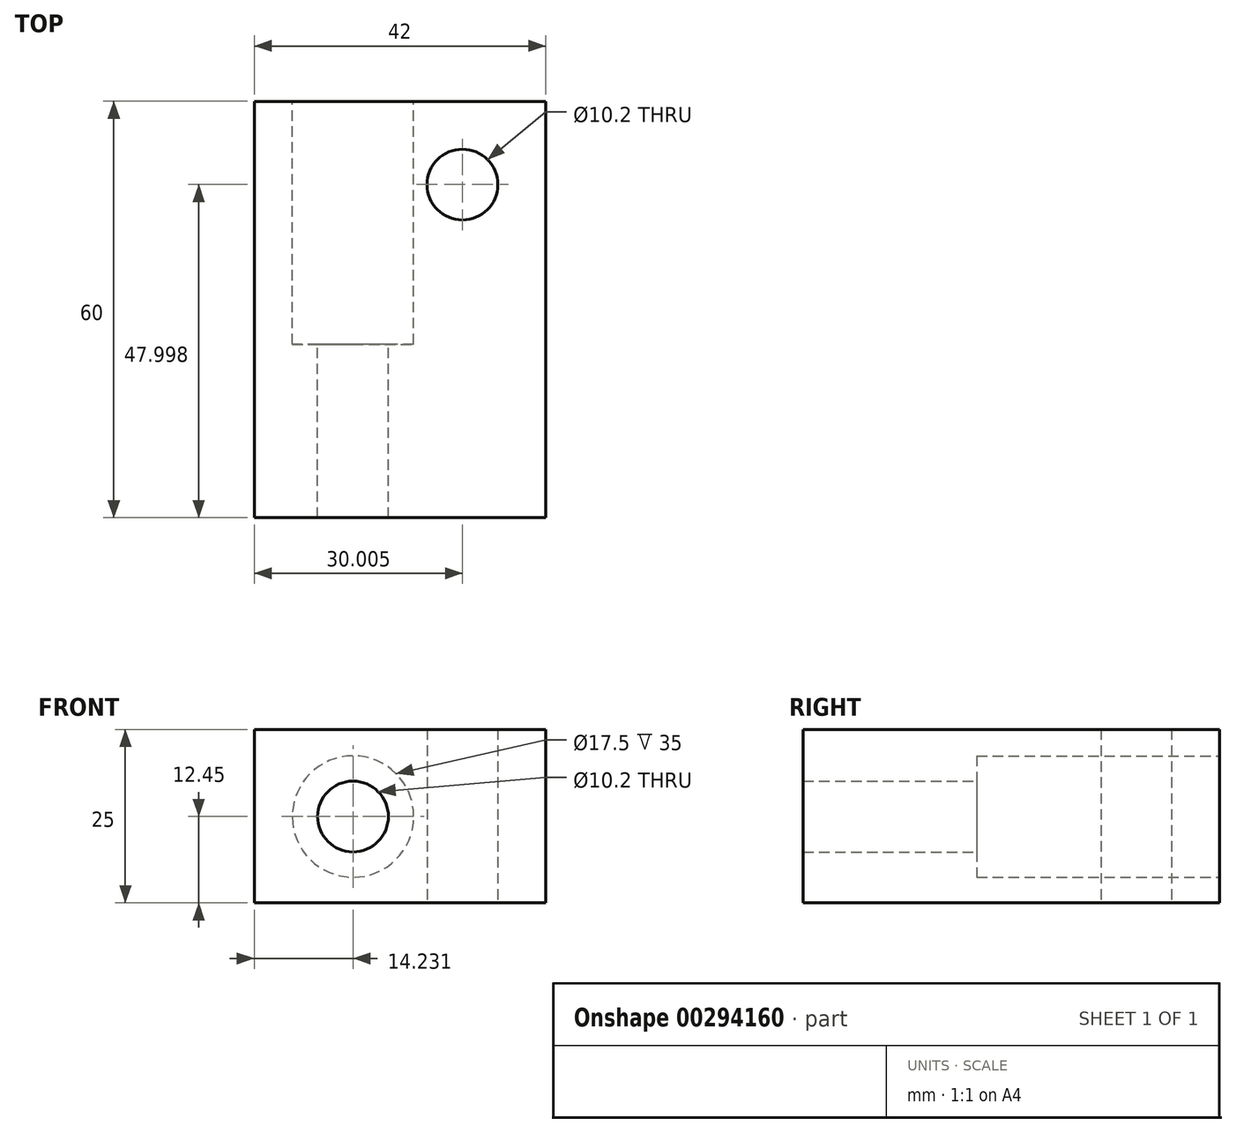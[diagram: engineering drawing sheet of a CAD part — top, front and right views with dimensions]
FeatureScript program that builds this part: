
annotation { "Feature Type Name" : "Feature", "Feature Type Description" : "" }
export const myFeature = defineFeature(function(context is Context, id is Id, definition is map)
    precondition{}
    {
        {
            var Q0;
            Q0=qCreatedBy(makeId("Top.planeOp"),FACE);
            var sketch = newSketch(context, id + "F0", { "sketchPlane" : qUnion([Q0])});
            skLineSegment(sketch, "E0", {"start": v(-36.42, -11.14) * mm, "end": v(5.58, -11.14) * mm});
            skLineSegment(sketch, "E1", {"start": v(5.58, -11.14) * mm, "end": v(5.58, 48.86) * mm});
            skLineSegment(sketch, "E2", {"start": v(5.58, 48.86) * mm, "end": v(-36.42, 48.86) * mm});
            skLineSegment(sketch, "E3", {"start": v(-36.42, 48.86) * mm, "end": v(-36.42, -11.14) * mm});
            skLineSegment(sketch, "E4", {"start": v(5.58, 48.86) * mm, "end": v(-6.42, 48.86) * mm});
            skLineSegment(sketch, "E5", {"start": v(-6.42, 48.86) * mm, "end": v(-6.42, 36.86) * mm, "construction": true});
            skCircle(sketch, "E6", {"center": v(-6.42, 36.86) * mm, "radius": 5.1 * mm});
            skSolve(sketch);
        }
        {
            var Q0;
            Q0=makeQuery(id+"F0.imprint","IMPRINT",FACE,{"disambiguationData":[TD([[makeQuery(id+"F0.imprint","IMPRINT",EDGE,{"derivedFrom":sQuery(id+"F0.wireOp",EDGE,"E0")}),1.0]])]});
            extrude(context, id + "F1", {"entities" : qUnion([Q0]), "depth" : 25 * mm});
        }
        {
            var Q0;
            Q0=makeQuery(id+"F1.opExtrude","SWEPT_FACE",FACE,{"disambiguationData":[OSD([sQuery(id+"F0.wireOp",EDGE,"E2"),sQuery(id+"F0.wireOp",EDGE,"E4")])]});
            var sketch = newSketch(context, id + "F2", { "sketchPlane" : qUnion([Q0])});
            skCircle(sketch, "E7", {"center": v(22.19, 12.45) * mm, "radius": 8.75 * mm});
            skCircle(sketch, "E8", {"center": v(22.19, 12.45) * mm, "radius": 5.1 * mm});
            skSolve(sketch);
        }
        {
            var Q0;
            Q0 = qSketchRegion(id + "F2", true);
            extrude(context, id + "F3", {"entities" : qUnion([Q0]), "operationType" : NewBodyOperationType.REMOVE, "oppositeDirection" : true, "depth" : 35 * mm});
        }
        {
            var Q0;
            Q0=makeQuery(id+"F3.boolean.opBoolean","SPLIT",FACE,{"disambiguationData":[TD([makeQuery(id+"F3.opExtrude","SWEPT_FACE",FACE,{"disambiguationData":[OSD([sQuery(id+"F2.wireOp",EDGE,"E8")])]})])],"derivedFrom":makeQuery(id+"F1.opExtrude","SWEPT_FACE",FACE,{"disambiguationData":[OSD([sQuery(id+"F0.wireOp",EDGE,"E2"),sQuery(id+"F0.wireOp",EDGE,"E4")])]})});
            extrude(context, id + "F4", {"entities" : qUnion([Q0]), "operationType" : NewBodyOperationType.REMOVE, "oppositeDirection" : true, "depth" : 60 * mm});
        }
    });
